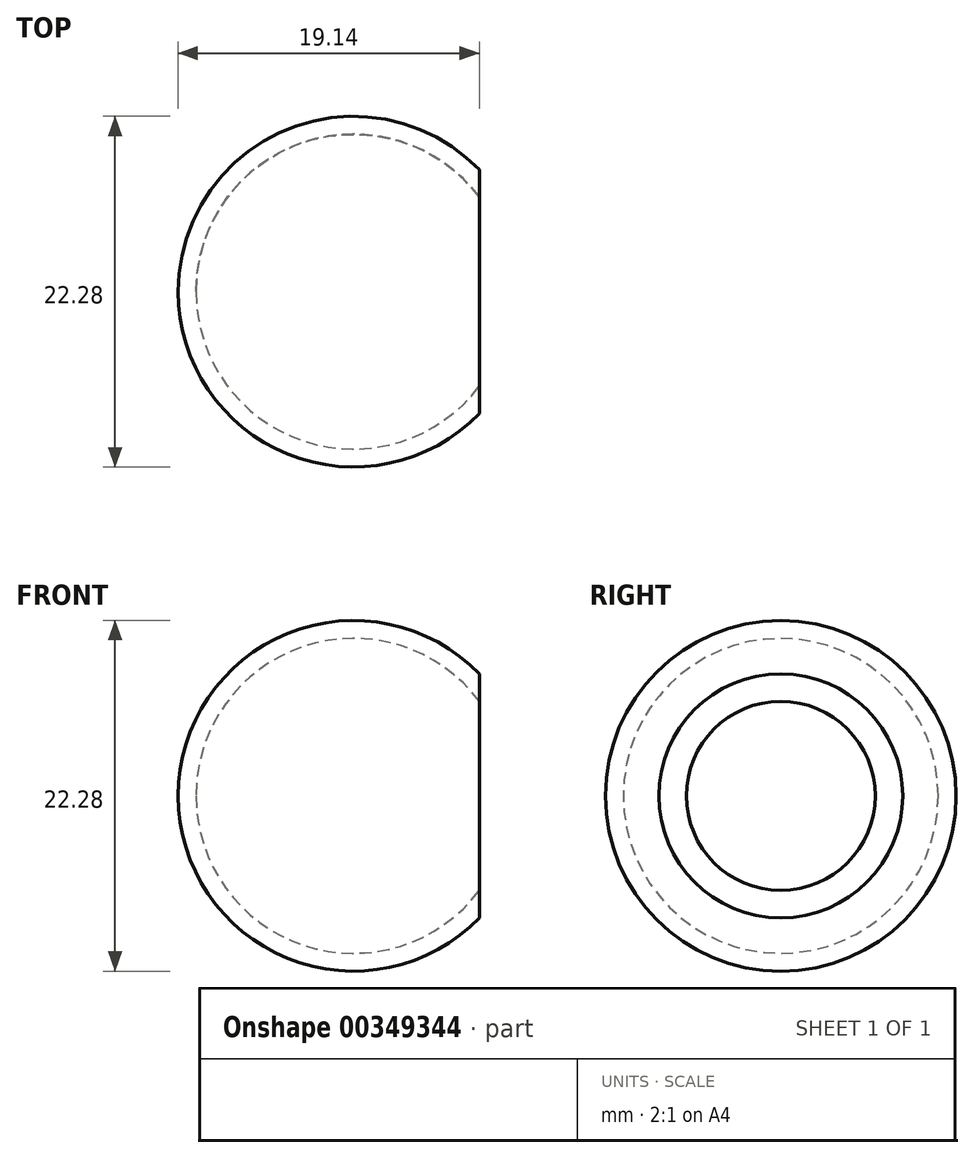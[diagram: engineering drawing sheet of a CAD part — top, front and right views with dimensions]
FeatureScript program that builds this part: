
annotation { "Feature Type Name" : "Feature", "Feature Type Description" : "" }
export const myFeature = defineFeature(function(context is Context, id is Id, definition is map)
    precondition{}
    {
        {
            var Q0;
            Q0=qCreatedBy(makeId("Top.planeOp"),FACE);
            var sketch = newSketch(context, id + "F0", { "sketchPlane" : qUnion([Q0])});
            skCircle(sketch, "E0", {"center": v(0, 0) * mm, "radius": 10 * mm});
            skCircle(sketch, "E1", {"center": v(0, 0) * mm, "radius": 11.14 * mm});
            skLineSegment(sketch, "E2", {"start": v(0, 0) * mm, "end": v(0, -11.14) * mm});
            skLineSegment(sketch, "E3", {"start": v(0, 0) * mm, "end": v(0, 11.14) * mm});
            skLineSegment(sketch, "E4", {"start": v(0, 0) * mm, "end": v(10, 0) * mm, "construction": true});
            skLineSegment(sketch, "E5", {"start": v(10, 0) * mm, "end": v(11.14, 0) * mm, "construction": true});
            skLineSegment(sketch, "E6", {"start": v(8.66, -5) * mm, "end": v(8.66, 5) * mm});
            skLineSegment(sketch, "E7", {"start": v(0, 0) * mm, "end": v(-11.14, 0) * mm});
            skLineSegment(sketch, "E8.bottom", {"start": v(8.66, -5) * mm, "end": v(8, -5) * mm});
            skLineSegment(sketch, "E8.top", {"start": v(8.66, 7.75) * mm, "end": v(8, 7.75) * mm});
            skLineSegment(sketch, "E8.left", {"start": v(8.66, -5) * mm, "end": v(8.66, 7.75) * mm});
            skLineSegment(sketch, "E8.right", {"start": v(8, -5) * mm, "end": v(8, 7.75) * mm});
            skLineSegment(sketch, "E9", {"start": v(8.66, 5) * mm, "end": v(8, 5) * mm});
            skLineSegment(sketch, "E10", {"start": v(8, 5) * mm, "end": v(8, 6) * mm});
            skLineSegment(sketch, "E11", {"start": v(8.66, 5) * mm, "end": v(8.66, 7) * mm});
            skSolve(sketch);
        }
        {
            var Q0;
            {var subQ3=sQuery(id+"F0.wireOp",EDGE,"E3");var subQ5=sQuery(id+"F0.wireOp",EDGE,"E1");var subQ6=makeQuery(id+"F0.imprint","INTERSECT",VERTEX,{"derivedFrom":[subQ5,subQ3]});Q0=makeQuery(id+"F0.imprint","IMPRINT",FACE,{"disambiguationData":[TD([[makeQuery(id+"F0.imprint","IMPRINT",EDGE,{"disambiguationData":[TD([[subQ6,1.0]])],"derivedFrom":subQ3}),-1.0]])]});}
            var Q1;
            {var subQ0=sQuery(id+"F0.wireOp",EDGE,"E3");var subQ1=sQuery(id+"F0.wireOp",EDGE,"E0");var subQ2=makeQuery(id+"F0.imprint","INTERSECT",VERTEX,{"derivedFrom":[subQ1,subQ0]});Q1=makeQuery(id+"F0.imprint","IMPRINT",FACE,{"disambiguationData":[TD([[makeQuery(id+"F0.imprint","IMPRINT",EDGE,{"disambiguationData":[TD([[subQ2,-1.0]])],"derivedFrom":subQ1}),-1.0]])]});}
            var Q2;
            Q2=sQuery(id+"F0.wireOp",EDGE,"E7");
            revolve(context, id + "F1", {"entities" : qUnion([Q0, Q1]), "axis" : qUnion([Q2]), "revolveType" : RevolveType.FULL});
        }
    });
